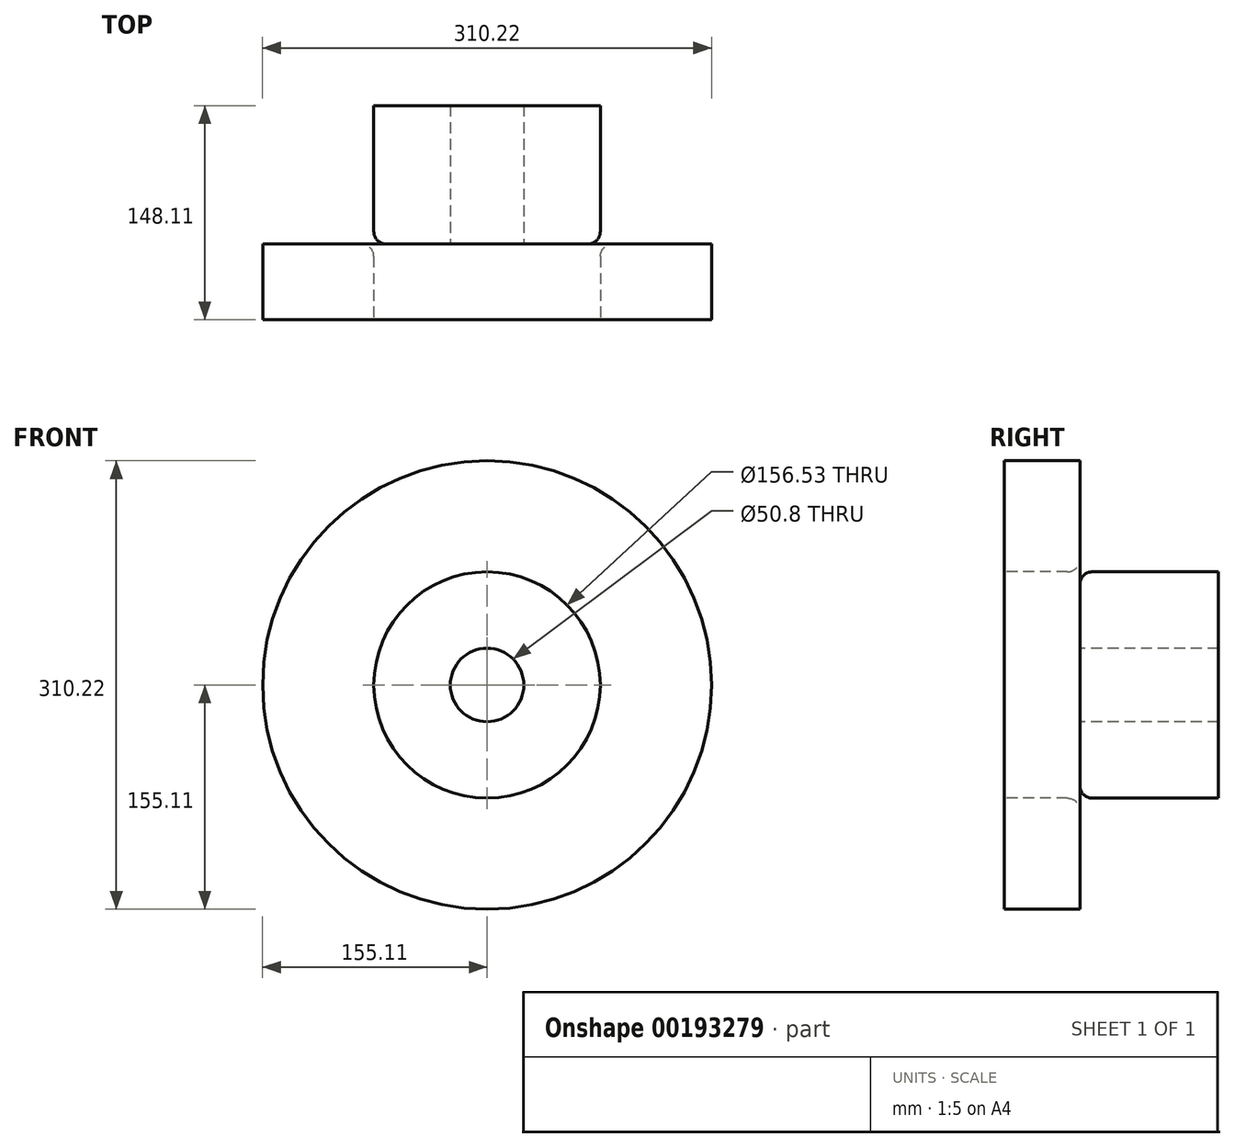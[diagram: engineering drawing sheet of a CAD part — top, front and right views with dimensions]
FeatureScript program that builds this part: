
annotation { "Feature Type Name" : "Feature", "Feature Type Description" : "" }
export const myFeature = defineFeature(function(context is Context, id is Id, definition is map)
    precondition{}
    {
        {
            var Q0;
            Q0=qCreatedBy(makeId("Right.planeOp"),FACE);
            var sketch = newSketch(context, id + "F0", { "sketchPlane" : qUnion([Q0])});
            skLineSegment(sketch, "E0", {"start": v(0, 0) * mm, "end": v(148.11, 0) * mm});
            skLineSegment(sketch, "E1.bottom", {"start": v(0, 25.4) * mm, "end": v(52.32, 25.4) * mm});
            skLineSegment(sketch, "E1.top", {"start": v(0, 155.1) * mm, "end": v(52.32, 155.1) * mm});
            skLineSegment(sketch, "E1.left", {"start": v(0, 25.4) * mm, "end": v(0, 155.1) * mm});
            skLineSegment(sketch, "E1.right", {"start": v(52.32, 25.4) * mm, "end": v(52.32, 155.1) * mm});
            skLineSegment(sketch, "E2.bottom", {"start": v(0, 25.4) * mm, "end": v(148.11, 25.4) * mm});
            skLineSegment(sketch, "E2.top", {"start": v(0, 78.26) * mm, "end": v(148.11, 78.26) * mm});
            skLineSegment(sketch, "E2.left", {"start": v(0, 25.4) * mm, "end": v(0, 78.26) * mm});
            skLineSegment(sketch, "E2.right", {"start": v(148.11, 25.4) * mm, "end": v(148.11, 78.26) * mm});
            skLineSegment(sketch, "E3.MirrorCS", {"start": v(0, -25.4) * mm, "end": v(52.32, -25.4) * mm});
            skLineSegment(sketch, "E4.MirrorCS", {"start": v(148.11, -25.4) * mm, "end": v(148.11, -78.26) * mm});
            skLineSegment(sketch, "E5.MirrorCS", {"start": v(0, -25.4) * mm, "end": v(0, -155.1) * mm});
            skLineSegment(sketch, "E6.MirrorCS", {"start": v(0, -25.4) * mm, "end": v(0, -78.26) * mm});
            skLineSegment(sketch, "E7.MirrorCS", {"start": v(0, -25.4) * mm, "end": v(148.11, -25.4) * mm});
            skLineSegment(sketch, "E8.MirrorCS", {"start": v(52.32, -25.4) * mm, "end": v(52.32, -155.1) * mm});
            skLineSegment(sketch, "E9.MirrorCS", {"start": v(0, -155.1) * mm, "end": v(52.32, -155.1) * mm});
            skLineSegment(sketch, "E10.MirrorCS", {"start": v(0, -78.26) * mm, "end": v(148.11, -78.26) * mm});
            skSolve(sketch);
        }
        {
            var Q0;
            {var subQ0=sQuery(id+"F0.wireOp",EDGE,"E1.top");Q0=makeQuery(id+"F0.imprint","IMPRINT",FACE,{"disambiguationData":[TD([[makeQuery(id+"F0.imprint","IMPRINT",EDGE,{"derivedFrom":subQ0}),-1.0]])]});}
            var Q1;
            {var subQ5=sQuery(id+"F0.wireOp",EDGE,"E2.left");Q1=makeQuery(id+"F0.imprint","IMPRINT",FACE,{"disambiguationData":[TD([[makeQuery(id+"F0.imprint","IMPRINT",EDGE,{"derivedFrom":subQ5}),-1.0]])]});}
            var Q2;
            {var subQ5=sQuery(id+"F0.wireOp",EDGE,"E2.right");Q2=makeQuery(id+"F0.imprint","IMPRINT",FACE,{"disambiguationData":[TD([[makeQuery(id+"F0.imprint","IMPRINT",EDGE,{"derivedFrom":subQ5}),1.0]])]});}
            var Q3;
            Q3=sQuery(id+"F0.wireOp",EDGE,"E0");
            revolve(context, id + "F1", {"entities" : qUnion([Q0, Q1, Q2]), "axis" : qUnion([Q3]), "revolveType" : RevolveType.FULL});
        }
        {
            var Q0;
            Q0=makeQuery(id+"F1.opRevolve","SWEPT_EDGE",EDGE,{"disambiguationData":[OSD([sQuery(id+"F0.wireOp",EDGE,"E1.right"),sQuery(id+"F0.wireOp",EDGE,"E2.top")])]});
            fillet(context, id + "F2", {"entities" : qUnion([Q0]), "radius" : 8.58 * mm, "tangentPropagation" : true, "allowEdgeOverflow" : false});
        }
    });
